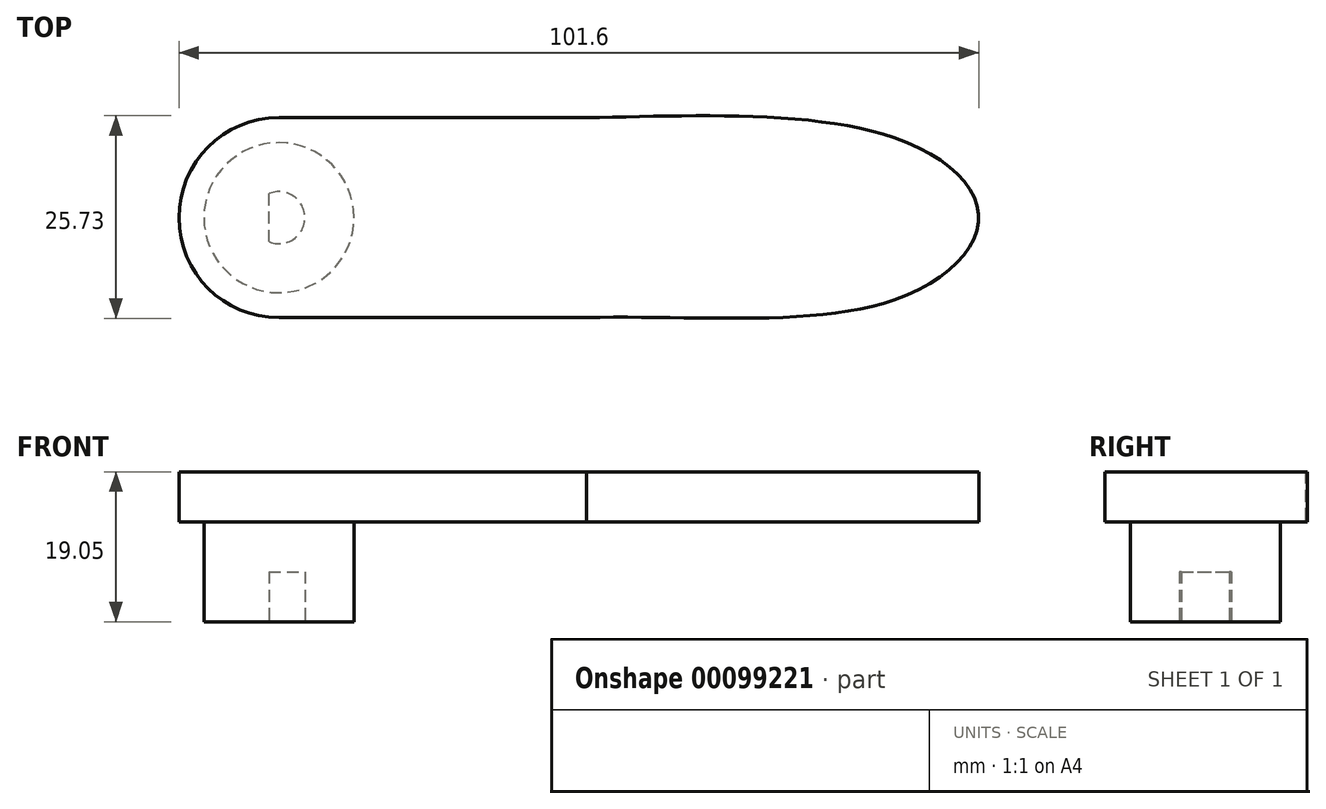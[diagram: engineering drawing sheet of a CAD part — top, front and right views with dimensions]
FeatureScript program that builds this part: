
annotation { "Feature Type Name" : "Feature", "Feature Type Description" : "" }
export const myFeature = defineFeature(function(context is Context, id is Id, definition is map)
    precondition{}
    {
        {
            var Q0;
            Q0=qCreatedBy(makeId("Top.planeOp"),FACE);
            var sketch = newSketch(context, id + "F0", { "sketchPlane" : qUnion([Q0])});
            skArc(sketch, "E0", {"start": v(-1.27, -3.05) * mm, "mid": v(3.3, 0) * mm, "end": v(-1.27, 3.05) * mm});
            skLineSegment(sketch, "E1", {"start": v(-1.27, -8.83) * mm, "end": v(-1.27, 11.1) * mm});
            skSolve(sketch);
        }
        {
            var Q0;
            Q0=qCreatedBy(makeId("Top.planeOp"),FACE);
            var sketch = newSketch(context, id + "F1", { "sketchPlane" : qUnion([Q0])});
            skCircle(sketch, "E2", {"center": v(0, 0) * mm, "radius": 9.53 * mm});
            skSolve(sketch);
        }
        {
            var Q0;
            Q0 = qSketchRegion(id + "F1", true);
            extrude(context, id + "F2", {"entities" : qUnion([Q0]), "depth" : 12.7 * mm});
        }
        {
            var Q0;
            Q0 = qSketchRegion(id + "F0", true);
            extrude(context, id + "F3", {"entities" : qUnion([Q0]), "operationType" : NewBodyOperationType.REMOVE, "depth" : 6.35 * mm});
        }
        {
            var Q0;
            Q0=makeQuery(id+"F2.opExtrude","CAP_FACE",FACE,{"disambiguationData":[OSD([sQuery(id+"F1.wireOp",EDGE,"E2")])],"isStart":false});
            var sketch = newSketch(context, id + "F4", { "sketchPlane" : qUnion([Q0])});
            skCircle(sketch, "E3", {"center": v(0, 0) * mm, "radius": 12.7 * mm});
            skLineSegment(sketch, "E4.bottom", {"start": v(0, 12.7) * mm, "end": v(39.07, 12.7) * mm});
            skLineSegment(sketch, "E4.top", {"start": v(0, -12.7) * mm, "end": v(39.07, -12.7) * mm});
            skLineSegment(sketch, "E4.left", {"start": v(0, 12.7) * mm, "end": v(0, -12.7) * mm});
            skLineSegment(sketch, "E4.right", {"start": v(78.15, 10.17) * mm, "end": v(78.15, -10.47) * mm});
            skFitSpline(sketch, "E5", {"points": [v(39.07, 12.7) * mm, v(78.15, 10.17) * mm, v(88.9, 0) * mm, v(78.15, -10.47) * mm, v(39.07, -12.7) * mm], "startDerivative": vector(120.08, 2.24) * mm, "endDerivative": vector(-126.1, -3.76) * mm});
            skPoint(sketch, "E6.orphan", {"position": v(78.15, 12.7) * mm});
            skPoint(sketch, "E7.orphan", {"position": v(78.15, -12.7) * mm});
            skSolve(sketch);
        }
        {
            var Q0;
            {var subQ0=sQuery(id+"F4.wireOp",EDGE,"E4.right");Q0=makeQuery(id+"F4.imprint","IMPRINT",FACE,{"disambiguationData":[TD([[makeQuery(id+"F4.imprint","IMPRINT",EDGE,{"derivedFrom":subQ0}),1.0]])]});}
            var Q1;
            {var subQ0=sQuery(id+"F4.wireOp",EDGE,"E4.top");Q1=makeQuery(id+"F4.imprint","IMPRINT",FACE,{"disambiguationData":[TD([[makeQuery(id+"F4.imprint","IMPRINT",EDGE,{"derivedFrom":subQ0}),1.0]])]});}
            var Q2;
            {var subQ0=sQuery(id+"F4.wireOp",EDGE,"E4.left");var subQ4=makeQuery(id+"F2.opExtrude","CAP_EDGE",EDGE,{"disambiguationData":[OSD([sQuery(id+"F1.wireOp",EDGE,"E2")])],"isStart":false});var subQ5=makeQuery(id+"F4.imprint","INTERSECT",VERTEX,{"disambiguationData":[OD(0.0)],"derivedFrom":[subQ4,subQ0]});Q2=makeQuery(id+"F4.imprint","IMPRINT",FACE,{"disambiguationData":[TD([[makeQuery(id+"F4.imprint","IMPRINT",EDGE,{"disambiguationData":[TD([[subQ5,-1.0]])],"derivedFrom":subQ4}),-1.0]])]});}
            var Q3;
            {var subQ0=sQuery(id+"F4.wireOp",EDGE,"E4.left");var subQ4=makeQuery(id+"F2.opExtrude","CAP_EDGE",EDGE,{"disambiguationData":[OSD([sQuery(id+"F1.wireOp",EDGE,"E2")])],"isStart":false});var subQ5=makeQuery(id+"F4.imprint","INTERSECT",VERTEX,{"disambiguationData":[OD(0.0)],"derivedFrom":[subQ4,subQ0]});Q3=makeQuery(id+"F4.imprint","IMPRINT",FACE,{"disambiguationData":[TD([[makeQuery(id+"F4.imprint","IMPRINT",EDGE,{"disambiguationData":[TD([[subQ5,1.0]])],"derivedFrom":subQ4}),-1.0]])]});}
            var Q4;
            {var subQ0=sQuery(id+"F4.wireOp",EDGE,"E4.left");var subQ1=makeQuery(id+"F2.opExtrude","CAP_EDGE",EDGE,{"disambiguationData":[OSD([sQuery(id+"F1.wireOp",EDGE,"E2")])],"isStart":false});var subQ2=makeQuery(id+"F4.imprint","INTERSECT",VERTEX,{"disambiguationData":[OD(0.0)],"derivedFrom":[subQ1,subQ0]});Q4=makeQuery(id+"F4.imprint","IMPRINT",FACE,{"disambiguationData":[TD([[makeQuery(id+"F4.imprint","IMPRINT",EDGE,{"disambiguationData":[TD([[subQ2,-1.0]])],"derivedFrom":subQ0}),1.0]])]});}
            var Q5;
            {var subQ0=sQuery(id+"F4.wireOp",EDGE,"E4.left");var subQ1=makeQuery(id+"F2.opExtrude","CAP_EDGE",EDGE,{"disambiguationData":[OSD([sQuery(id+"F1.wireOp",EDGE,"E2")])],"isStart":false});var subQ2=makeQuery(id+"F4.imprint","INTERSECT",VERTEX,{"disambiguationData":[OD(0.0)],"derivedFrom":[subQ1,subQ0]});Q5=makeQuery(id+"F4.imprint","IMPRINT",FACE,{"disambiguationData":[TD([[makeQuery(id+"F4.imprint","IMPRINT",EDGE,{"disambiguationData":[TD([[subQ2,-1.0]])],"derivedFrom":subQ0}),-1.0]])]});}
            extrude(context, id + "F5", {"entities" : qUnion([Q0, Q1, Q2, Q3, Q4, Q5]), "operationType" : NewBodyOperationType.ADD, "depth" : 6.35 * mm});
        }
    });
